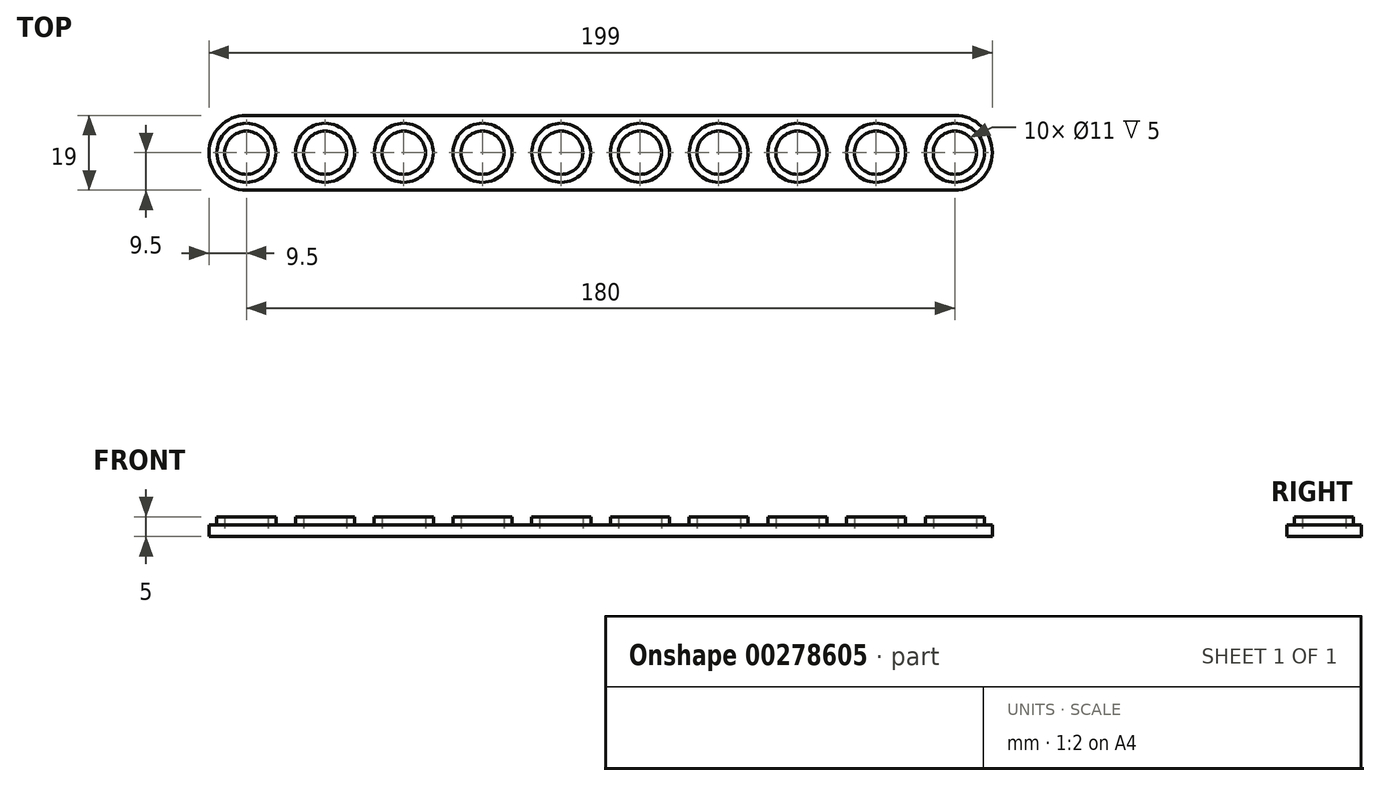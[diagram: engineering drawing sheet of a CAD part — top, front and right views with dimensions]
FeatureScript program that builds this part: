
annotation { "Feature Type Name" : "Feature", "Feature Type Description" : "" }
export const myFeature = defineFeature(function(context is Context, id is Id, definition is map)
    precondition{}
    {
        {
            assignVariable(context, id + "F0", {"name" : "e", "anyValue" : 3});
        }
        {
            assignVariable(context, id + "F1", {"name" : "h0", "anyValue" : 2});
        }
        {
            var Q0;
            Q0=qCreatedBy(makeId("Top.planeOp"),FACE);
            var sketch = newSketch(context, id + "F2", { "sketchPlane" : qUnion([Q0])});
            skLineSegment(sketch, "E0.bottom", {"start": v(0, 9.5) * mm, "end": v(180, 9.5) * mm});
            skLineSegment(sketch, "E0.top", {"start": v(0, -9.5) * mm, "end": v(180, -9.5) * mm});
            skLineSegment(sketch, "E0.left", {"start": v(-9.5, 0) * mm, "end": v(-9.5, 0) * mm});
            skLineSegment(sketch, "E0.right", {"start": v(189.5, 0) * mm, "end": v(189.5, 0) * mm});
            skPoint(sketch, "E1", {"position": v(-9.5, 0) * mm});
            skCircle(sketch, "E2", {"center": v(0, 0) * mm, "radius": 5.5 * mm});
            skPoint(sketch, "E3.visualSharp", {"position": v(189.5, 9.5) * mm});
            skArc(sketch, "E3.filletArc", {"start": v(189.5, 0) * mm, "mid": v(186.72, 6.72) * mm, "end": v(180, 9.5) * mm});
            skPoint(sketch, "E4.visualSharp", {"position": v(189.5, -9.5) * mm});
            skArc(sketch, "E4.filletArc", {"start": v(180, -9.5) * mm, "mid": v(186.72, -6.72) * mm, "end": v(189.5, 0) * mm});
            skPoint(sketch, "E5.visualSharp", {"position": v(-9.5, -9.5) * mm});
            skArc(sketch, "E5.filletArc", {"start": v(-9.5, 0) * mm, "mid": v(-6.72, -6.72) * mm, "end": v(0, -9.5) * mm});
            skPoint(sketch, "E6.visualSharp", {"position": v(-9.5, 9.5) * mm});
            skArc(sketch, "E6.filletArc", {"start": v(0, 9.5) * mm, "mid": v(-6.72, 6.72) * mm, "end": v(-9.5, 0) * mm});
            skCircle(sketch, "E7", {"center": v(0, 0) * mm, "radius": 7.5 * mm});
            skCircle(sketch, "E8.1.0.0", {"center": v(20, 0) * mm, "radius": 5.5 * mm});
            skCircle(sketch, "E8.1.0.1", {"center": v(20, 0) * mm, "radius": 7.5 * mm});
            skCircle(sketch, "E8.2.0.0", {"center": v(40, 0) * mm, "radius": 5.5 * mm});
            skCircle(sketch, "E8.2.0.1", {"center": v(40, 0) * mm, "radius": 7.5 * mm});
            skLineSegment(sketch, "E8.direction1", {"start": v(0, 0) * mm, "end": v(20, 0) * mm, "construction": true});
            skCircle(sketch, "E9.0.3.0", {"center": v(60, 0) * mm, "radius": 5.5 * mm});
            skCircle(sketch, "E9.2.3.0", {"center": v(60, 0) * mm, "radius": 7.5 * mm});
            skCircle(sketch, "E9.0.4.0", {"center": v(80, 0) * mm, "radius": 5.5 * mm});
            skCircle(sketch, "E9.2.4.0", {"center": v(80, 0) * mm, "radius": 7.5 * mm});
            skCircle(sketch, "E9.0.5.0", {"center": v(100, 0) * mm, "radius": 5.5 * mm});
            skCircle(sketch, "E9.2.5.0", {"center": v(100, 0) * mm, "radius": 7.5 * mm});
            skCircle(sketch, "E9.0.6.0", {"center": v(120, 0) * mm, "radius": 5.5 * mm});
            skCircle(sketch, "E9.2.6.0", {"center": v(120, 0) * mm, "radius": 7.5 * mm});
            skCircle(sketch, "E9.0.7.0", {"center": v(140, 0) * mm, "radius": 5.5 * mm});
            skCircle(sketch, "E9.2.7.0", {"center": v(140, 0) * mm, "radius": 7.5 * mm});
            skCircle(sketch, "E9.0.8.0", {"center": v(160, 0) * mm, "radius": 5.5 * mm});
            skCircle(sketch, "E9.2.8.0", {"center": v(160, 0) * mm, "radius": 7.5 * mm});
            skCircle(sketch, "E9.0.9.0", {"center": v(180, 0) * mm, "radius": 5.5 * mm});
            skCircle(sketch, "E9.2.9.0", {"center": v(180, 0) * mm, "radius": 7.5 * mm});
            skSolve(sketch);
        }
        {
            var Q0;
            Q0=qSketchRegion(id+"F2",true);
            var Q1;
            Q1=makeQuery(id+"F2.imprint","IMPRINT",FACE,{"disambiguationData":[TD([[makeQuery(id+"F2.imprint","IMPRINT",EDGE,{"derivedFrom":sQuery(id+"F2.wireOp",EDGE,"E2")}),-1.0]])]});
            var Q2;
            Q2=makeQuery(id+"F2.imprint","IMPRINT",FACE,{"disambiguationData":[TD([[makeQuery(id+"F2.imprint","IMPRINT",EDGE,{"derivedFrom":sQuery(id+"F2.wireOp",EDGE,"E8.1.0.0")}),-1.0]])]});
            var Q3;
            Q3=makeQuery(id+"F2.imprint","IMPRINT",FACE,{"disambiguationData":[TD([[makeQuery(id+"F2.imprint","IMPRINT",EDGE,{"derivedFrom":sQuery(id+"F2.wireOp",EDGE,"E8.2.0.0")}),-1.0]])]});
            var Q4;
            Q4=makeQuery(id+"F2.imprint","IMPRINT",FACE,{"disambiguationData":[TD([[makeQuery(id+"F2.imprint","IMPRINT",EDGE,{"derivedFrom":sQuery(id+"F2.wireOp",EDGE,"345b2114-0edb-480d-a68f-e22b198684d9.0.3.0")}),-1.0]])]});
            var Q5;
            Q5=makeQuery(id+"F2.imprint","IMPRINT",FACE,{"disambiguationData":[TD([[makeQuery(id+"F2.imprint","IMPRINT",EDGE,{"derivedFrom":sQuery(id+"F2.wireOp",EDGE,"E9.0.3.0")}),-1.0]])]});
            var Q6;
            Q6=makeQuery(id+"F2.imprint","IMPRINT",FACE,{"disambiguationData":[TD([[makeQuery(id+"F2.imprint","IMPRINT",EDGE,{"derivedFrom":sQuery(id+"F2.wireOp",EDGE,"E9.0.4.0")}),-1.0]])]});
            var Q7;
            Q7=makeQuery(id+"F2.imprint","IMPRINT",FACE,{"disambiguationData":[TD([[makeQuery(id+"F2.imprint","IMPRINT",EDGE,{"derivedFrom":sQuery(id+"F2.wireOp",EDGE,"E9.0.5.0")}),-1.0]])]});
            var Q8;
            Q8=makeQuery(id+"F2.imprint","IMPRINT",FACE,{"disambiguationData":[TD([[makeQuery(id+"F2.imprint","IMPRINT",EDGE,{"derivedFrom":sQuery(id+"F2.wireOp",EDGE,"E9.0.6.0")}),-1.0]])]});
            var Q9;
            Q9=makeQuery(id+"F2.imprint","IMPRINT",FACE,{"disambiguationData":[TD([[makeQuery(id+"F2.imprint","IMPRINT",EDGE,{"derivedFrom":sQuery(id+"F2.wireOp",EDGE,"E9.0.7.0")}),-1.0]])]});
            var Q10;
            Q10=makeQuery(id+"F2.imprint","IMPRINT",FACE,{"disambiguationData":[TD([[makeQuery(id+"F2.imprint","IMPRINT",EDGE,{"derivedFrom":sQuery(id+"F2.wireOp",EDGE,"E9.0.8.0")}),-1.0]])]});
            var Q11;
            Q11=makeQuery(id+"F2.imprint","IMPRINT",FACE,{"disambiguationData":[TD([[makeQuery(id+"F2.imprint","IMPRINT",EDGE,{"derivedFrom":sQuery(id+"F2.wireOp",EDGE,"E9.0.9.0")}),-1.0]])]});
            extrude(context, id + "F3", {"entities" : qUnion([Q0, Q1, Q2, Q3, Q4, Q5, Q6, Q7, Q8, Q9, Q10, Q11]), "depth" : (getVariable(context, 'e')) * mm});
        }
        {
            var Q0;
            Q0=makeQuery(id+"F2.imprint","IMPRINT",FACE,{"disambiguationData":[TD([[makeQuery(id+"F2.imprint","IMPRINT",EDGE,{"derivedFrom":sQuery(id+"F2.wireOp",EDGE,"E2")}),-1.0]])]});
            var Q1;
            Q1=makeQuery(id+"F2.imprint","IMPRINT",FACE,{"disambiguationData":[TD([[makeQuery(id+"F2.imprint","IMPRINT",EDGE,{"derivedFrom":sQuery(id+"F2.wireOp",EDGE,"E8.1.0.0")}),-1.0]])]});
            var Q2;
            Q2=makeQuery(id+"F2.imprint","IMPRINT",FACE,{"disambiguationData":[TD([[makeQuery(id+"F2.imprint","IMPRINT",EDGE,{"derivedFrom":sQuery(id+"F2.wireOp",EDGE,"E8.2.0.0")}),-1.0]])]});
            var Q3;
            Q3=makeQuery(id+"F2.imprint","IMPRINT",FACE,{"disambiguationData":[TD([[makeQuery(id+"F2.imprint","IMPRINT",EDGE,{"derivedFrom":sQuery(id+"F2.wireOp",EDGE,"345b2114-0edb-480d-a68f-e22b198684d9.0.3.0")}),-1.0]])]});
            var Q4;
            Q4=makeQuery(id+"F2.imprint","IMPRINT",FACE,{"disambiguationData":[TD([[makeQuery(id+"F2.imprint","IMPRINT",EDGE,{"derivedFrom":sQuery(id+"F2.wireOp",EDGE,"E9.0.3.0")}),-1.0]])]});
            var Q5;
            Q5=makeQuery(id+"F2.imprint","IMPRINT",FACE,{"disambiguationData":[TD([[makeQuery(id+"F2.imprint","IMPRINT",EDGE,{"derivedFrom":sQuery(id+"F2.wireOp",EDGE,"E9.0.4.0")}),-1.0]])]});
            var Q6;
            Q6=makeQuery(id+"F2.imprint","IMPRINT",FACE,{"disambiguationData":[TD([[makeQuery(id+"F2.imprint","IMPRINT",EDGE,{"derivedFrom":sQuery(id+"F2.wireOp",EDGE,"E9.0.5.0")}),-1.0]])]});
            var Q7;
            Q7=makeQuery(id+"F2.imprint","IMPRINT",FACE,{"disambiguationData":[TD([[makeQuery(id+"F2.imprint","IMPRINT",EDGE,{"derivedFrom":sQuery(id+"F2.wireOp",EDGE,"E9.0.6.0")}),-1.0]])]});
            var Q8;
            Q8=makeQuery(id+"F2.imprint","IMPRINT",FACE,{"disambiguationData":[TD([[makeQuery(id+"F2.imprint","IMPRINT",EDGE,{"derivedFrom":sQuery(id+"F2.wireOp",EDGE,"E9.0.7.0")}),-1.0]])]});
            var Q9;
            Q9=makeQuery(id+"F2.imprint","IMPRINT",FACE,{"disambiguationData":[TD([[makeQuery(id+"F2.imprint","IMPRINT",EDGE,{"derivedFrom":sQuery(id+"F2.wireOp",EDGE,"E9.0.8.0")}),-1.0]])]});
            var Q10;
            Q10=makeQuery(id+"F2.imprint","IMPRINT",FACE,{"disambiguationData":[TD([[makeQuery(id+"F2.imprint","IMPRINT",EDGE,{"derivedFrom":sQuery(id+"F2.wireOp",EDGE,"E9.0.9.0")}),-1.0]])]});
            extrude(context, id + "F4", {"entities" : qUnion([Q0, Q1, Q2, Q3, Q4, Q5, Q6, Q7, Q8, Q9, Q10]), "operationType" : NewBodyOperationType.ADD, "depth" : (getVariable(context, 'e') + getVariable(context, 'h0')) * mm});
        }
    });
